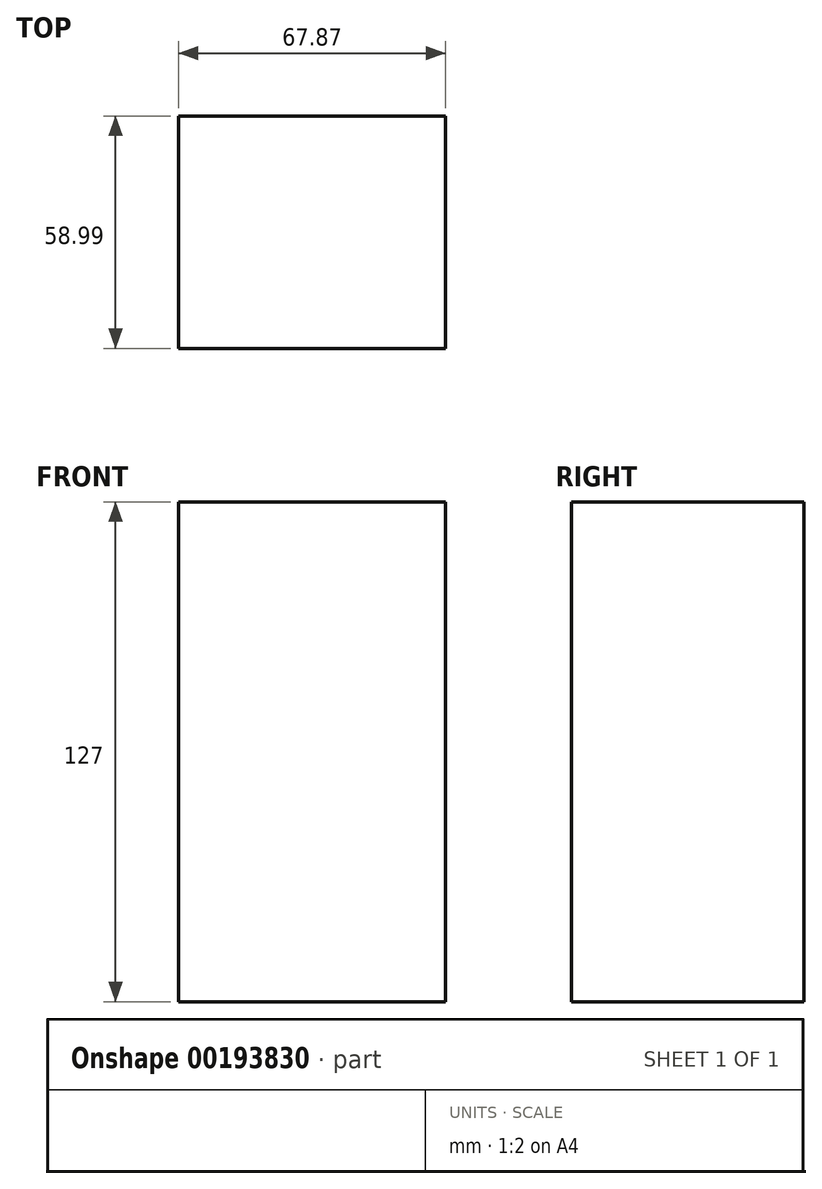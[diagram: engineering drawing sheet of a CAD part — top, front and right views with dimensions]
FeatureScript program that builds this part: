
annotation { "Feature Type Name" : "Feature", "Feature Type Description" : "" }
export const myFeature = defineFeature(function(context is Context, id is Id, definition is map)
    precondition{}
    {
        {
            var Q0;
            Q0=qCreatedBy(makeId("Top.planeOp"),FACE);
            var sketch = newSketch(context, id + "F1", { "sketchPlane" : qUnion([Q0])});
            skLineSegment(sketch, "E0.bottom", {"start": v(-31.52, 26.21) * mm, "end": v(36.35, 26.21) * mm});
            skLineSegment(sketch, "E0.top", {"start": v(-31.52, -32.78) * mm, "end": v(36.35, -32.78) * mm});
            skLineSegment(sketch, "E0.left", {"start": v(-31.52, 26.21) * mm, "end": v(-31.52, -32.78) * mm});
            skLineSegment(sketch, "E0.right", {"start": v(36.35, 26.21) * mm, "end": v(36.35, -32.78) * mm});
            skSolve(sketch);
        }
        {
            var Q0;
            Q0=makeQuery(id+"F1.imprint","IMPRINT",FACE,{"disambiguationData":[TD([[makeQuery(id+"F1.imprint","IMPRINT",EDGE,{"derivedFrom":sQuery(id+"F1.wireOp",EDGE,"E0.bottom")}),-1.0]])]});
            var sketch = newSketch(context, id + "F2", { "sketchPlane" : qUnion([Q0])});
            skSolve(sketch);
        }
        {
            var Q0;
            Q0=makeQuery(id+"F2.imprint","IMPRINT",FACE,{"disambiguationData":[TD([[makeQuery(id+"F2.imprint","IMPRINT",EDGE,{"derivedFrom":makeQuery(id+"F1.imprint","IMPRINT",EDGE,{"derivedFrom":sQuery(id+"F1.wireOp",EDGE,"E0.bottom")})}),-1.0]])]});
            var Q1;
            Q1=makeQuery(id+"F1.imprint","IMPRINT",FACE,{"disambiguationData":[TD([[makeQuery(id+"F1.imprint","IMPRINT",EDGE,{"derivedFrom":sQuery(id+"F1.wireOp",EDGE,"E0.bottom")}),-1.0]])]});
            extrude(context, id + "F3", {"entities" : qUnion([Q0, Q1]), "depth" : 127 * mm});
        }
    });
